# Revit family: Spaces In Between_Play
name_source: partatom
category: Furniture Systems
units: mm (PartAtom-declared; Revit-internal decimal feet)

## family parameters
Always vertical = Yes
Cut with Voids When Loaded = No
Part Type = Normal
Room Calculation Point = No
Round Connector Dimension = Use Diameter
Shared = No
Work Plane-Based = No

## types (1)
- Spaces In Between_Play
    Curved Corner Side Fabric - 1 = <By Category>
    Curved Corner Side Fabric - 2 = <By Category>
    Curved Corner Side Fabric - 3 = <By Category>
    Curved Corner Side Fabric - 4 = <By Category>
    Curved Corner Step 1 Fabric - 1 = <By Category>
    Curved Corner Step 1 Fabric - 2 = <By Category>
    Curved Corner Step 1 Fabric - 3 = <By Category>
    Curved Corner Step 1 Fabric - 4 = <By Category>
    Curved Corner Step 2 Fabric - 1 = <By Category>
    Curved Corner Step 2 Fabric - 2 = <By Category>
    Curved Corner Step 2 Fabric - 3 = <By Category>
    Curved Corner Step 2 Fabric - 4 = <By Category>
    Glide = <By Category>
    Manufacturer = FOMCORE
    Medium Hemisphere Ottoman Fabric = <By Category>
    Model = Spaces In Between_Play
    Small Hemisphere Ottoman Fabric - 1 = <By Category>
    Small Hemisphere Ottoman Fabric - 2 = <By Category>
    Three Step Series Back Fabric -1 = <By Category>
    Three Step Series Back Fabric -2 = <By Category>
    Three Step Series Side Fabric -1 = <By Category>
    Three Step Series Side Fabric -2 = <By Category>
    Three Step Series Step 1 Fabric -1 = <By Category>
    Three Step Series Step 1 Fabric -2 = <By Category>
    Three Step Series Step 2 Fabric -1 = <By Category>
    Three Step Series Step 2 Fabric -2 = <By Category>
    Three Step Series Step 3 Fabric -1 = <By Category>
    Three Step Series Step 3 Fabric -2 = <By Category>
    Two Step Series Side Fabric -1 = <By Category>
    Two Step Series Side Fabric -2 = <By Category>
    Two Step Series Step 1 Fabric -1 = <By Category>
    Two Step Series Step 1 Fabric -2 = <By Category>
    Two Step Series Step 2 Fabric -1 = <By Category>
    Two Step Series Step 2 Fabric -2 = <By Category>
    Type Comments = COMBO UNIT
    URL = https://fomcore.com

## geometry (parser evidence)
native form markers: Sweep x18
no freeform markers — native parametric forms only
